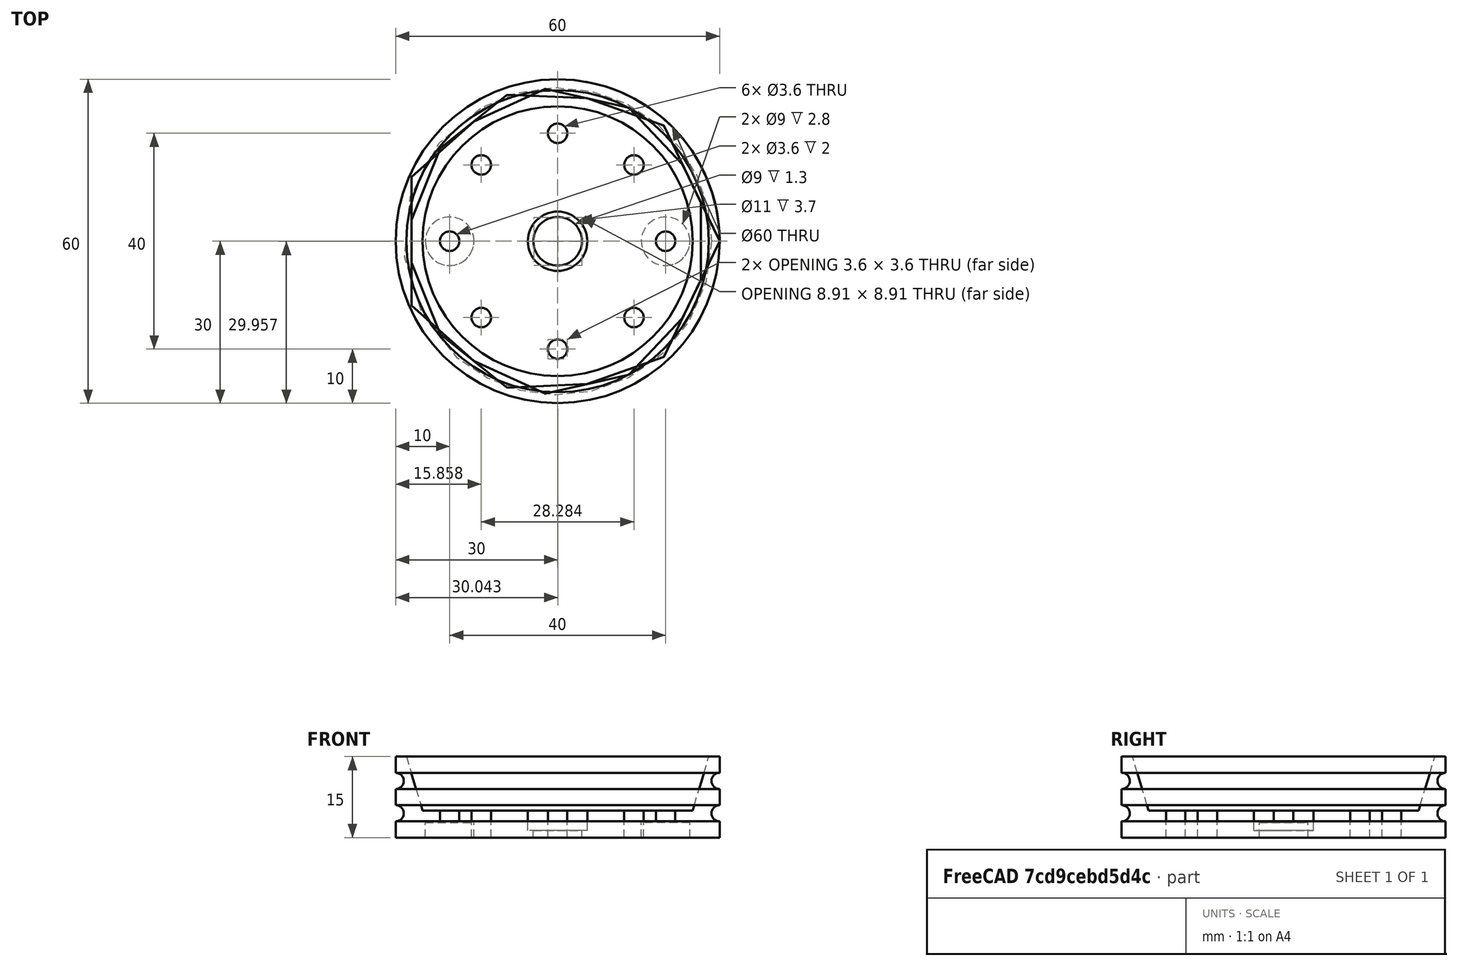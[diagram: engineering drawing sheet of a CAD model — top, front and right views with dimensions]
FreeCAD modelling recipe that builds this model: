
FCSTD DOCUMENT  (FreeCAD 0.14R3702 (Git))
Label: wheel-rear
License: CC-BY 3.0
LicenseURL: http://creativecommons.org/licenses/by/3.0/
objects: Part::Cylinder×6, Part::Cut×6, Part::FeaturePython×4, Part::Cone×1, Part::MultiFuse×1, Part::Torus×1
note: 19 computed .brp shape members not serialized (recipe doc carries the construction recipe); baked Part::Feature solids carry a one-line shape summary decoded from their .brp

FEATURE [Part::Cylinder] Cylinder  label="base-cylinder"
  Angle = 360
  Height = 15
  Radius = 30
FEATURE [Part::Cone] Cone  label="conic-cutout"
  Angle = 360
  Height = 10
  Placement = pos=(0,0,15) rot=(0,1,0;3.14159rad)
  Radius1 = 28
  Radius2 = 25
FEATURE [Part::Cut] Cut  label="wheel-with-cutout"
  Base = -> Cylinder
  Tool = -> Cone
FEATURE [Part::Cylinder] Cylinder001  label="drill-master"
  Angle = 360
  Height = 10
  Placement = pos=(20,0,-2) rot=(0,0,1;0rad)
  Radius = 1.8
FEATURE [Part::FeaturePython] Array  label="Cylinders-array-drills"  # Draft array (typed FeaturePython)
  Angle = 360
  ArrayType = 1
  Axis = (0,0,1)
  Base = -> Cylinder001
  Center = (0,0,0)
  IntervalX = (1,0,0)
  IntervalY = (0,1,0)
  IntervalZ = (0,0,1)
  NumberPolar = 8
  NumberX = 2
  NumberY = 2
  NumberZ = 1
FEATURE [Part::Cylinder] Cylinder002  label="inner-cutout-4.5mm"
  Angle = 360
  Height = 10
  Placement = pos=(0,0,1.3) rot=(0,0,1;0rad)
  Radius = 5.5
FEATURE [Part::Cylinder] Cylinder003  label="cylinder-inner-shaft"
  Angle = 360
  Height = 14
  Placement = pos=(0,0,-1) rot=(0,0,1;0rad)
  Radius = 4.5
FEATURE [Part::Cut] Cut001  label="wheel-2"
  Base = -> Cut
  Tool = -> Cylinder002
FEATURE [Part::Cut] Cut002  label="wheel-3-with-shaft"
  Base = -> Cut001
  Tool = -> Cylinder003
FEATURE [Part::Cut] Cut003  label="wheel-4-drills"
  Base = -> Cut002
  Tool = -> Array
FEATURE [Part::Cylinder] Cylinder004  label="slot_9mm_master"
  Angle = 360
  Height = 10
  Placement = pos=(20,0,-9) rot=(0,0,1;0rad)
  Radius = 4.5
FEATURE [Part::FeaturePython] Array001  label="Cutout-for-screws-cap"  # Draft array (typed FeaturePython)
  Angle = 360
  ArrayType = 1
  Axis = (0,0,1)
  Base = -> Cylinder004
  Center = (0,0,0)
  IntervalX = (1,0,0)
  IntervalY = (0,1,0)
  IntervalZ = (0,0,1)
  NumberPolar = 2
  NumberX = 2
  NumberY = 2
  NumberZ = 1
  Placement = pos=(0,0,2) rot=(0,0,1;0rad)
FEATURE [Part::Cut] Cut004  label="wheel-5"
  Base = -> Cut003
  Tool = -> Array001
FEATURE [Part::Cylinder] Cylinder004001  label="slot-cover-master"
  Angle = 360
  Height = 0.2
  Placement = pos=(20,0,0.8) rot=(0,0,1;0rad)
  Radius = 4.5
FEATURE [Part::FeaturePython] Array002  label="cap-cover-thin"  # Draft array (typed FeaturePython)
  Angle = 360
  ArrayType = 1
  Axis = (0,0,1)
  Base = -> Cylinder004001
  Center = (0,0,0)
  IntervalX = (1,0,0)
  IntervalY = (0,1,0)
  IntervalZ = (0,0,1)
  NumberPolar = 2
  NumberX = 2
  NumberY = 2
  NumberZ = 1
  Placement = pos=(0,0,2) rot=(0,0,1;0rad)
FEATURE [Part::MultiFuse] Fusion  label="wheel-6"
  Shapes = -> [Cut004,Array002]
FEATURE [Part::Torus] Torus  label="Torus_master"
  Angle1 = -180
  Angle2 = 180
  Angle3 = 360
  Placement = pos=(0,0,-1.5) rot=(0,0,1;0rad)
  Radius1 = 30
  Radius2 = 1.5
FEATURE [Part::FeaturePython] Array003  label="Array_torus"  # Draft array (typed FeaturePython)
  Angle = 360
  ArrayType = 0
  Axis = (0,0,1)
  Base = -> Torus
  Center = (0,0,0)
  IntervalX = (1,0,0)
  IntervalY = (0,1,0)
  IntervalZ = (0,0,6)
  NumberPolar = 1
  NumberX = 1
  NumberY = 1
  NumberZ = 2
  Placement = pos=(0,0,6) rot=(0,0,1;0rad)
FEATURE [Part::Cut] Cut005  label="Wheel-rear"
  Base = -> Fusion
  Tool = -> Array003
